# Revit family: IS_Idealrain_BD140_BIM_NL
name_source: partatom
category: Plumbing Fixtures
units: mm (PartAtom-declared; Revit-internal decimal feet)

## family parameters
Always vertical = No
Cut with Voids When Loaded = No
OmniClass Number = 23.45.05.14.17
OmniClass Title = Showers
Part Type = Normal
Room Calculation Point = No
Round Connector Dimension = Use Diameter
Shared = No
Work Plane-Based = No

## types (2) — shared parameters
Accesoires = https://www.idealstandard.nl
Accessories = https://www.idealstandard.nl
Afmetingen = 200 x 200 x 57 mm
AfstandsEenheid = Millimeter
AreaUnits = Millimetres
Artikelomschrijving = IDEALRAIN S1 REGENDUSCHE RUND 200MM KUNSTSTOFF
Artikelreferentie = IDEALRAIN S1 RAIN SHOWER ROUND 200MM PLASTIC
Auteur = Ideal Standard
BIMObjectName = IS_IdealStandard_Showermixers_Idealrain_BD140
BIMobject category = Sanitary
BIMobject category code = Taps & Mixers
BIMobject main category = Sanitary
Bedieningkraan = Handbuch
Bedieningkraanwerk = drehen wissen
Beschrijvingdouchekop = Regenbrause
Beschrijvinggarantie = Herstellergarantie
BimObjectNaam = IS_IdealStandard_Showermixers_Idealrain_BD140
Brand = Ideal Standard
Brand url = http://www.idealstandard.nl
Breedte = 200.010361
ConnectionType = Installation
CurrencyUnit = €
CurrentRevision = 1
Date of publishing = 24/07/2021
Diepte = 200 mm
Douchebak = No
DurationUnit = Years
Edition number = 1
Garantieonderdelen = 5
Garantieunits = Jaren
GemaaktOp = 27/07/2021
HasIntegralShutOffDevice = No
Help = https://www.idealstandard.nl
Hoogte = 56.5057582315058
Hulp = https://www.idealstandard.nl
IFC Classification = Sanitary Terminal
IfcExportAs = IfcValveType
IfcExportType = MIXING
Installatieinstructies = https://www.idealstandard.nl
Installation instructions = https://www.idealstandard.nl
InstallationInstructions = https://www.idealstandard.nl
IsBuiltIn = No
IsHighPressure = No
LinearUnits = Millimetres
MaintenanceInformation = https://www.idealstandard.nl
Manufacturer = Ideal Standard
Manufacturer name = Ideal Standard
ManufacturerURL = https://www.idealstandard.nl
Materiaal = Messing
Material = Brass
Material main = Brass
Merk = Ideal Standard
ModelReference = IDEALRAIN S1 RAIN SHOWER ROUND 200MM PLASTIC
Montageinstuctie = https://www.idealstandard.nl
NBS Reference Code = 45-35-70/335
NBS Reference Description = Shower mixers
Name = Showermixers_Idealrain_BD140_IdealStandard
NettWeight = 0.49
Nettogewicht = 0.49
NominalDepth = 200 mm
NominalHeight = 57 mm
NominalLength = 200 mm
NominalWidth = 200 mm
Normen = Showermixers_Idealrain_BD140_IdealStandard
OppervlakteEenheid = Millimeter
Product Guid = d86534d5-f1b3-467f-bc2e-dbad6ff9b45b
Product SKU = BD140
Product certification = https://www.idealstandard.nl
Product data url = https://bimobject.com
Product family = Sanitary
Product group = Showers
Product name = IDEALRAIN S1 RAIN SHOWER ROUND 200MM PLASTIC
Product url = https://www.idealstandard.nl
ProductInformation = https://www.idealstandard.nl
ProductSoort = Sanitary
Productinformatie = https://www.idealstandard.nl
QR code = http://bimobject.com
Referentie = IDEALRAIN S1 RAIN SHOWER ROUND 200MM PLASTIC
Revisie = 1
Shape = Round
ShowerHeadDescription = Round Rain ShowerHead
Size = 200 x 200 x 57 mm
Space = Internal
SpareParts = https://www.idealstandard.nl
Technical description = https://www.idealstandard.nl
Telefoonnummer = 077 355 08 08
TestPressure = 10 Bar
Testdruk = 10 Bar
Typeconnectie = Installation
URL = https://www.idealstandard.nl
Uniclass 2015 Code = Pr_40_20_87_80
Uniclass 2015 Name = Shower thermostatic valves
Uniclass2015Beschrijving = Shower thermostatic valves
Uniclass2015Code = Pr_40_20_87_80
Uniclass2015Referentie = Pr_40_20_87_80
Uniclass2015Title = Shower thermostatic valves
Uniclass2015Version = v1.22
Urlproducent = https://www.idealstandard.nl
ValutaEenheid = Euro
Versie = 1
Version = 1
VolumeUnits = Litres
Volumeunits = Liters
Vorm = zylindrisch
WRASURL = https://www.wrasapprovals.co.uk
WarrantyDescription = Manufacturer warranty
WarrantyDurationUnit = Years
Wisselstukken = https://www.idealstandard.nl
Youtube clip = https://www.youtube.com
zero-valued in all types: BrutoGewicht, Cost, Lengte, Vervangingskosten

## per-type parameters (varying)
| type | Afwerking | Artikelnummer | BarCode | Barcode | Color | Description | Eigenschappen | Features | Finish | GTIN code | Kleur | MainColor | Model | ModelNumber |
| BD140AA - IDEALRAIN S1 RAIN SHOWER ROUND 200MM PLASTIC - CHROME | Chrom | BD140AA | 3800861108368 | 3800861108368 | Chrom | IDEALRAIN S1 REGENDUSCHE RUND 200MM KUNSTSTOFF - CHROM | S1 REGENDUSCHE RUND 200MM KUNSTSTOFF - CHROM | S1 REGENDUSCHE RUND 200MM KUNSTSTOFF - CHROM | Chrom | https://3800861108368 | Chrom | Chrom | BD140AA | BD140AA |
| BD140XG - IDEALRAIN S1 RAIN SHOWER ROUND 200MM PLASTIC - SILK BLACK | Seide schwarz | BD140XG | 3800861101109 | 3800861101109 | Seide schwarz | IDEALRAIN S1 REGENDUSCHE RUND 200MM KUNSTSTOFF - SEIDE SCHWARZ | S1 REGENDUSCHE RUND 200MM KUNSTSTOFF - SEIDE SCHWARZ | S1 REGENDUSCHE RUND 200MM KUNSTSTOFF - SEIDE SCHWARZ | Seide schwarz | https://3800861101109 | Seide schwarz | Seide schwarz | BD140XG | BD140XG |

## geometry (parser evidence)
native form markers: Sweep x3
no freeform markers — native parametric forms only
